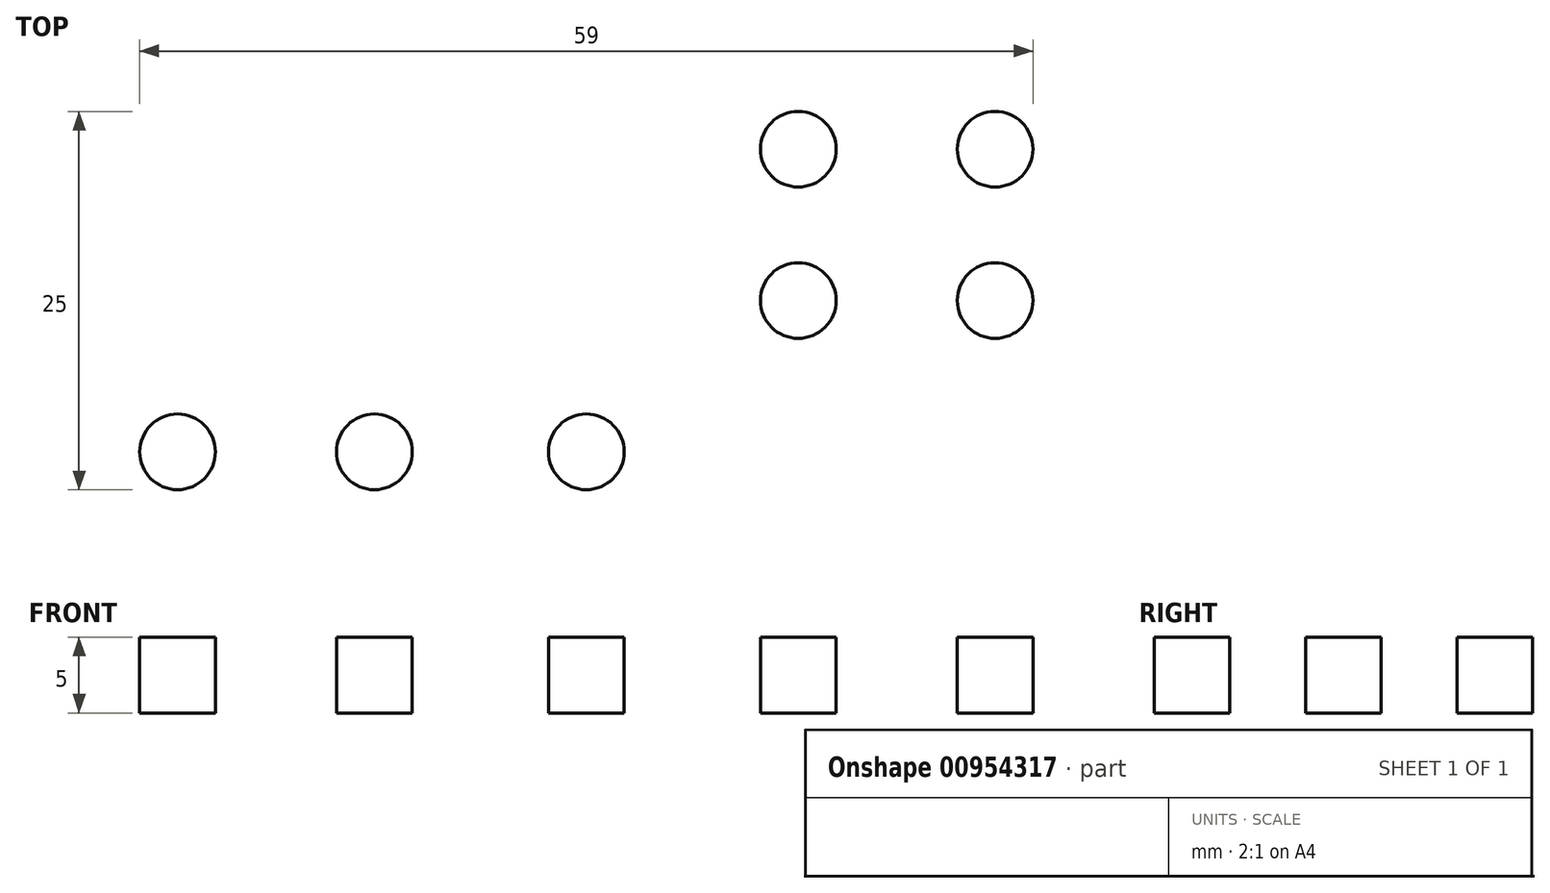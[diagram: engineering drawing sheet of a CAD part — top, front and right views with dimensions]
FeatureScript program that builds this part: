
annotation { "Feature Type Name" : "Feature", "Feature Type Description" : "" }
export const myFeature = defineFeature(function(context is Context, id is Id, definition is map)
    precondition{}
    {
        {
            var Q0;
            Q0=qCreatedBy(makeId("Top.planeOp"),FACE);
            var sketch = newSketch(context, id + "F0", { "sketchPlane" : qUnion([Q0])});
            skLineSegment(sketch, "E0.bottom", {"start": v(-40, 25) * mm, "end": v(40, 25) * mm});
            skLineSegment(sketch, "E0.top", {"start": v(-40, -25) * mm, "end": v(40, -25) * mm});
            skLineSegment(sketch, "E0.left", {"start": v(-40, 25) * mm, "end": v(-40, -25) * mm});
            skLineSegment(sketch, "E0.right", {"start": v(40, 25) * mm, "end": v(40, -25) * mm});
            skPoint(sketch, "E0.middle", {"position": v(0, 0) * mm});
            skLineSegment(sketch, "E1", {"start": v(-5, 25) * mm, "end": v(-5, 30) * mm});
            skLineSegment(sketch, "E2", {"start": v(-5, 30) * mm, "end": v(5, 30) * mm});
            skLineSegment(sketch, "E3", {"start": v(5, 30) * mm, "end": v(5, 25) * mm});
            skLineSegment(sketch, "E4", {"start": v(5, 25) * mm, "end": v(-5, 25) * mm});
            skLineSegment(sketch, "E5.MirrorCS", {"start": v(-5, -30) * mm, "end": v(5, -30) * mm});
            skLineSegment(sketch, "E6.MirrorCS", {"start": v(5, -25) * mm, "end": v(-5, -25) * mm});
            skLineSegment(sketch, "E7.MirrorCS", {"start": v(5, -30) * mm, "end": v(5, -25) * mm});
            skLineSegment(sketch, "E8.MirrorCS", {"start": v(-5, -25) * mm, "end": v(-5, -30) * mm});
            skLineSegment(sketch, "E9", {"start": v(-40, 5) * mm, "end": v(-45, 5) * mm});
            skLineSegment(sketch, "E10", {"start": v(-45, 5) * mm, "end": v(-45, -5) * mm});
            skLineSegment(sketch, "E11", {"start": v(-45, -5) * mm, "end": v(-40, -5) * mm});
            skLineSegment(sketch, "E12", {"start": v(-40, -5) * mm, "end": v(-40, 5) * mm});
            skLineSegment(sketch, "E13.MirrorCS", {"start": v(40, 5) * mm, "end": v(45, 5) * mm});
            skLineSegment(sketch, "E14.MirrorCS", {"start": v(45, 5) * mm, "end": v(45, -5) * mm});
            skLineSegment(sketch, "E15.MirrorCS", {"start": v(45, -5) * mm, "end": v(40, -5) * mm});
            skLineSegment(sketch, "E16.MirrorCS", {"start": v(40, -5) * mm, "end": v(40, 5) * mm});
            skSolve(sketch);
        }
        {
            var Q0;
            {var subQ7=sQuery(id+"F0.wireOp",EDGE,"E0.bottom");var subQ12=makeQuery(id+"F0.imprint","INTERSECT",VERTEX,{"derivedFrom":[subQ7,sQuery(id+"F0.wireOp",EDGE,"E3")]});Q0=makeQuery(id+"F0.imprint","IMPRINT",FACE,{"disambiguationData":[TD([[makeQuery(id+"F0.imprint","IMPRINT",EDGE,{"disambiguationData":[TD([[subQ12,-1.0]])],"derivedFrom":subQ7}),-1.0]])]});}
            var Q1;
            {var subQ2=sQuery(id+"F0.wireOp",EDGE,"E1");Q1=makeQuery(id+"F0.imprint","IMPRINT",FACE,{"disambiguationData":[TD([[makeQuery(id+"F0.imprint","IMPRINT",EDGE,{"derivedFrom":subQ2}),-1.0]])]});}
            var Q2;
            {var subQ2=sQuery(id+"F0.wireOp",EDGE,"E9");Q2=makeQuery(id+"F0.imprint","IMPRINT",FACE,{"disambiguationData":[TD([[makeQuery(id+"F0.imprint","IMPRINT",EDGE,{"derivedFrom":subQ2}),1.0]])]});}
            var Q3;
            Q3=makeQuery(id+"F0.imprint","IMPRINT",FACE,{"disambiguationData":[TD([[makeQuery(id+"F0.imprint","IMPRINT",EDGE,{"derivedFrom":sQuery(id+"F0.wireOp",EDGE,"E5.MirrorCS")}),1.0]])]});
            var Q4;
            {var subQ2=sQuery(id+"F0.wireOp",EDGE,"E13.MirrorCS");Q4=makeQuery(id+"F0.imprint","IMPRINT",FACE,{"disambiguationData":[TD([[makeQuery(id+"F0.imprint","IMPRINT",EDGE,{"derivedFrom":subQ2}),-1.0]])]});}
            extrude(context, id + "F1", {"entities" : qUnion([Q0, Q1, Q2, Q3, Q4]), "depth" : 5 * mm, "offsetDistance" : 25 * mm});
        }
        {
            var Q0;
            Q0=makeQuery(id+"F1.opExtrude","CAP_FACE",FACE,{"disambiguationData":[OSD([sQuery(id+"F0.wireOp",EDGE,"E0.bottom"),sQuery(id+"F0.wireOp",EDGE,"E0.top"),sQuery(id+"F0.wireOp",EDGE,"E0.left"),sQuery(id+"F0.wireOp",EDGE,"E0.right"),sQuery(id+"F0.wireOp",EDGE,"E1"),sQuery(id+"F0.wireOp",EDGE,"E2"),sQuery(id+"F0.wireOp",EDGE,"E3"),sQuery(id+"F0.wireOp",EDGE,"E5.MirrorCS"),sQuery(id+"F0.wireOp",EDGE,"E7.MirrorCS"),sQuery(id+"F0.wireOp",EDGE,"E8.MirrorCS"),sQuery(id+"F0.wireOp",EDGE,"E9"),sQuery(id+"F0.wireOp",EDGE,"E10"),sQuery(id+"F0.wireOp",EDGE,"E11"),sQuery(id+"F0.wireOp",EDGE,"E13.MirrorCS"),sQuery(id+"F0.wireOp",EDGE,"E14.MirrorCS"),sQuery(id+"F0.wireOp",EDGE,"E15.MirrorCS")])],"isStart":false});
            var sketch = newSketch(context, id + "F2", { "sketchPlane" : qUnion([Q0])});
            skPoint(sketch, "E17.middle", {"position": v(0, 0) * mm});
            skCircle(sketch, "E18", {"center": v(-27, 10) * mm, "radius": 2.5 * mm});
            skCircle(sketch, "E19", {"center": v(-14, 10) * mm, "radius": 2.5 * mm});
            skCircle(sketch, "E20", {"center": v(0, 10) * mm, "radius": 2.5 * mm});
            skCircle(sketch, "E21.MirrorC", {"center": v(27, 10) * mm, "radius": 2.5 * mm});
            skCircle(sketch, "E22.MirrorC", {"center": v(14, 10) * mm, "radius": 2.5 * mm});
            skCircle(sketch, "E23.MirrorC", {"center": v(-27, -10) * mm, "radius": 2.5 * mm});
            skCircle(sketch, "E24.MirrorC", {"center": v(-14, -10) * mm, "radius": 2.5 * mm});
            skCircle(sketch, "E25.MirrorC", {"center": v(0, -10) * mm, "radius": 2.5 * mm});
            skCircle(sketch, "E26.MirrorC", {"center": v(14, -10) * mm, "radius": 2.5 * mm});
            skCircle(sketch, "E27.MirrorC", {"center": v(27, -10) * mm, "radius": 2.5 * mm});
            skCircle(sketch, "E28", {"center": v(-27, 0) * mm, "radius": 2.5 * mm});
            skCircle(sketch, "E29", {"center": v(-14, 0) * mm, "radius": 2.5 * mm});
            skCircle(sketch, "E30", {"center": v(0, 0) * mm, "radius": 2.5 * mm});
            skCircle(sketch, "E31.MirrorC", {"center": v(27, 0) * mm, "radius": 2.5 * mm});
            skCircle(sketch, "E32.MirrorC", {"center": v(14, 0) * mm, "radius": 2.5 * mm});
            skSolve(sketch);
        }
        {
            var Q0;
            Q0=makeQuery(id+"F2.imprint","IMPRINT",FACE,{"disambiguationData":[TD([[makeQuery(id+"F2.imprint","IMPRINT",EDGE,{"derivedFrom":sQuery(id+"F2.wireOp",EDGE,"E18")}),1.0]])]});
            var Q1;
            Q1=makeQuery(id+"F2.imprint","IMPRINT",FACE,{"disambiguationData":[TD([[makeQuery(id+"F2.imprint","IMPRINT",EDGE,{"derivedFrom":sQuery(id+"F2.wireOp",EDGE,"E19")}),1.0]])]});
            var Q2;
            Q2=makeQuery(id+"F2.imprint","IMPRINT",FACE,{"disambiguationData":[TD([[makeQuery(id+"F2.imprint","IMPRINT",EDGE,{"derivedFrom":sQuery(id+"F2.wireOp",EDGE,"E20")}),1.0]])]});
            var Q3;
            Q3=makeQuery(id+"F2.imprint","IMPRINT",FACE,{"disambiguationData":[TD([[makeQuery(id+"F2.imprint","IMPRINT",EDGE,{"derivedFrom":sQuery(id+"F2.wireOp",EDGE,"E22.MirrorC")}),-1.0]])]});
            var Q4;
            Q4=makeQuery(id+"F2.imprint","IMPRINT",FACE,{"disambiguationData":[TD([[makeQuery(id+"F2.imprint","IMPRINT",EDGE,{"derivedFrom":sQuery(id+"F2.wireOp",EDGE,"E21.MirrorC")}),-1.0]])]});
            var Q5;
            Q5=makeQuery(id+"F2.imprint","IMPRINT",FACE,{"disambiguationData":[TD([[makeQuery(id+"F2.imprint","IMPRINT",EDGE,{"derivedFrom":sQuery(id+"F2.wireOp",EDGE,"E28")}),1.0]])]});
            var Q6;
            Q6=makeQuery(id+"F2.imprint","IMPRINT",FACE,{"disambiguationData":[TD([[makeQuery(id+"F2.imprint","IMPRINT",EDGE,{"derivedFrom":sQuery(id+"F2.wireOp",EDGE,"E29")}),1.0]])]});
            var Q7;
            Q7=makeQuery(id+"F2.imprint","IMPRINT",FACE,{"disambiguationData":[TD([[makeQuery(id+"F2.imprint","IMPRINT",EDGE,{"derivedFrom":sQuery(id+"F2.wireOp",EDGE,"E30")}),1.0]])]});
            var Q8;
            Q8=makeQuery(id+"F2.imprint","IMPRINT",FACE,{"disambiguationData":[TD([[makeQuery(id+"F2.imprint","IMPRINT",EDGE,{"derivedFrom":sQuery(id+"F2.wireOp",EDGE,"E32.MirrorC")}),-1.0]])]});
            var Q9;
            Q9=makeQuery(id+"F2.imprint","IMPRINT",FACE,{"disambiguationData":[TD([[makeQuery(id+"F2.imprint","IMPRINT",EDGE,{"derivedFrom":sQuery(id+"F2.wireOp",EDGE,"E31.MirrorC")}),-1.0]])]});
            var Q10;
            Q10=makeQuery(id+"F2.imprint","IMPRINT",FACE,{"disambiguationData":[TD([[makeQuery(id+"F2.imprint","IMPRINT",EDGE,{"derivedFrom":sQuery(id+"F2.wireOp",EDGE,"E27.MirrorC")}),1.0]])]});
            var Q11;
            Q11=makeQuery(id+"F2.imprint","IMPRINT",FACE,{"disambiguationData":[TD([[makeQuery(id+"F2.imprint","IMPRINT",EDGE,{"derivedFrom":sQuery(id+"F2.wireOp",EDGE,"E26.MirrorC")}),1.0]])]});
            var Q12;
            Q12=makeQuery(id+"F2.imprint","IMPRINT",FACE,{"disambiguationData":[TD([[makeQuery(id+"F2.imprint","IMPRINT",EDGE,{"derivedFrom":sQuery(id+"F2.wireOp",EDGE,"E25.MirrorC")}),-1.0]])]});
            var Q13;
            Q13=makeQuery(id+"F2.imprint","IMPRINT",FACE,{"disambiguationData":[TD([[makeQuery(id+"F2.imprint","IMPRINT",EDGE,{"derivedFrom":sQuery(id+"F2.wireOp",EDGE,"E24.MirrorC")}),-1.0]])]});
            var Q14;
            Q14=makeQuery(id+"F2.imprint","IMPRINT",FACE,{"disambiguationData":[TD([[makeQuery(id+"F2.imprint","IMPRINT",EDGE,{"derivedFrom":sQuery(id+"F2.wireOp",EDGE,"E23.MirrorC")}),-1.0]])]});
            extrude(context, id + "F3", {"entities" : qUnion([Q0, Q1, Q2, Q3, Q4, Q5, Q6, Q7, Q8, Q9, Q10, Q11, Q12, Q13, Q14]), "operationType" : NewBodyOperationType.REMOVE, "oppositeDirection" : true, "depth" : 5 * mm, "offsetDistance" : 25 * mm});
        }
    });
